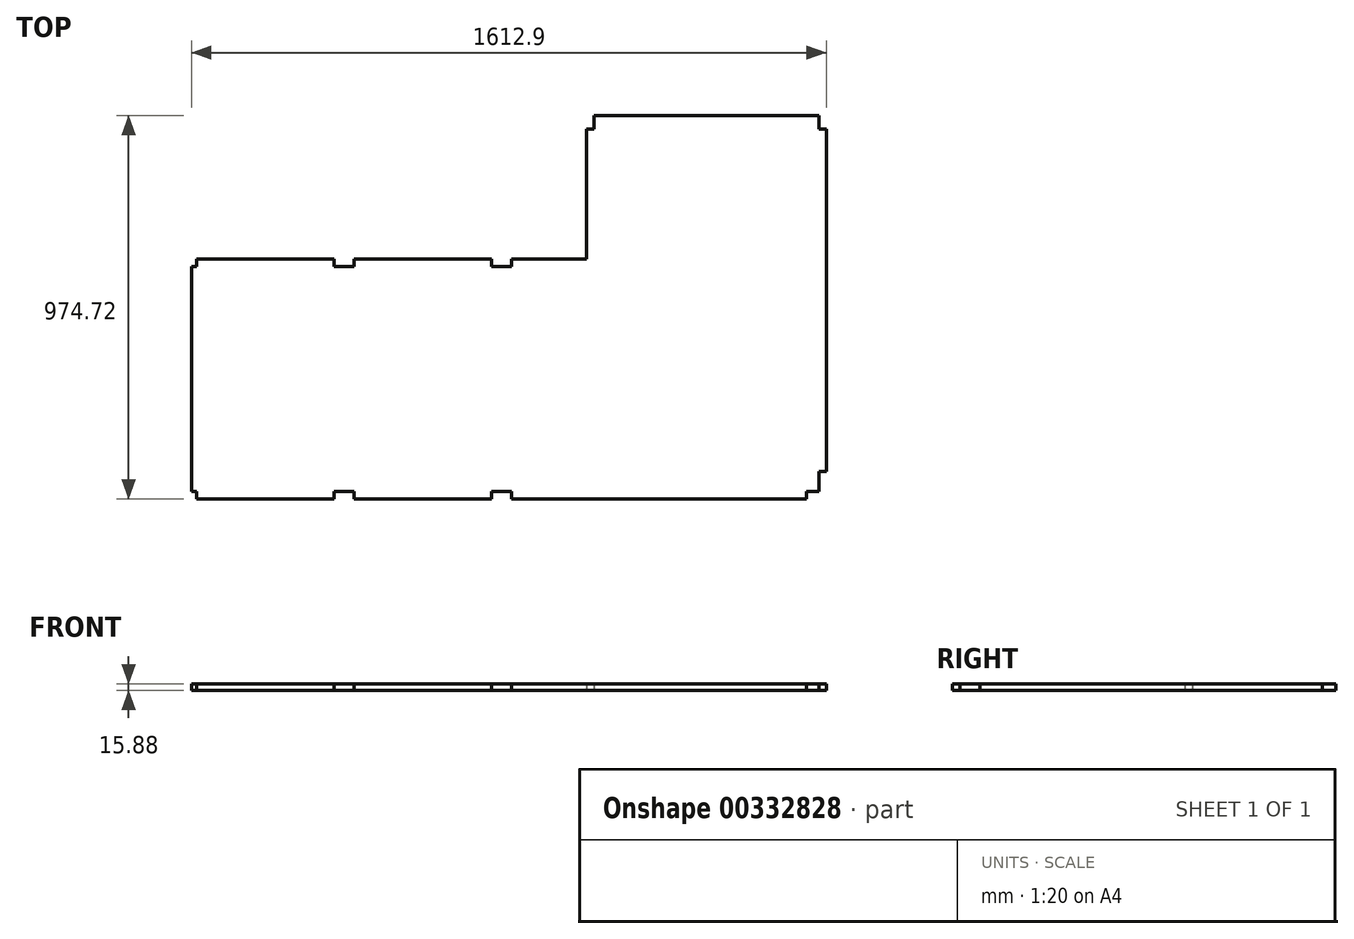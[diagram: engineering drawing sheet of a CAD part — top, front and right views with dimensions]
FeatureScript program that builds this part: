
annotation { "Feature Type Name" : "Feature", "Feature Type Description" : "" }
export const myFeature = defineFeature(function(context is Context, id is Id, definition is map)
    precondition{}
    {
        {
            var Q0;
            Q0=qCreatedBy(makeId("Top.planeOp"),FACE);
            var sketch = newSketch(context, id + "F0", { "sketchPlane" : qUnion([Q0])});
            skLineSegment(sketch, "E0.bottom", {"start": v(-50.8, 0) * mm, "end": v(-800.1, 0) * mm});
            skLineSegment(sketch, "E0.top", {"start": v(-19.05, 974.73) * mm, "end": v(-590.55, 974.72) * mm});
            skLineSegment(sketch, "E0.left", {"start": v(0, 69.85) * mm, "end": v(0, 939.8) * mm});
            skLineSegment(sketch, "E1.top", {"start": v(-1600.2, 609.6) * mm, "end": v(-1250.95, 609.6) * mm});
            skLineSegment(sketch, "E1.right", {"start": v(-609.6, 939.8) * mm, "end": v(-609.6, 609.6) * mm});
            skLineSegment(sketch, "E2.top", {"start": v(-1612.9, 590.55) * mm, "end": v(-1600.2, 590.55) * mm});
            skLineSegment(sketch, "E2.right", {"start": v(-1600.2, 609.6) * mm, "end": v(-1600.2, 590.55) * mm});
            skLineSegment(sketch, "E3.bottom", {"start": v(-1612.9, 19.05) * mm, "end": v(-1600.2, 19.05) * mm});
            skLineSegment(sketch, "E3.right", {"start": v(-1600.2, 19.05) * mm, "end": v(-1600.2, 0) * mm});
            skLineSegment(sketch, "E4.top", {"start": v(-609.6, 939.8) * mm, "end": v(-590.55, 939.8) * mm});
            skLineSegment(sketch, "E4.right", {"start": v(-590.55, 974.72) * mm, "end": v(-590.55, 939.8) * mm});
            skLineSegment(sketch, "E5.top", {"start": v(0, 939.8) * mm, "end": v(-19.05, 939.8) * mm});
            skLineSegment(sketch, "E5.right", {"start": v(-19.05, 974.73) * mm, "end": v(-19.05, 939.8) * mm});
            skLineSegment(sketch, "E6.top", {"start": v(-850.9, 590.55) * mm, "end": v(-800.1, 590.55) * mm});
            skLineSegment(sketch, "E6.left", {"start": v(-850.9, 609.6) * mm, "end": v(-850.9, 590.55) * mm});
            skLineSegment(sketch, "E6.right", {"start": v(-800.1, 609.6) * mm, "end": v(-800.1, 590.55) * mm});
            skLineSegment(sketch, "E7.trimOffspring", {"start": v(-800.1, 609.6) * mm, "end": v(-609.6, 609.6) * mm});
            skLineSegment(sketch, "E8.bottom", {"start": v(-850.9, 19.05) * mm, "end": v(-800.1, 19.05) * mm});
            skLineSegment(sketch, "E8.left", {"start": v(-850.9, 19.05) * mm, "end": v(-850.9, 0) * mm});
            skLineSegment(sketch, "E8.right", {"start": v(-800.1, 19.05) * mm, "end": v(-800.1, 0) * mm});
            skLineSegment(sketch, "E9.trimOffspring", {"start": v(-850.9, 0) * mm, "end": v(-1200.15, 0) * mm});
            skPoint(sketch, "E10.orphan", {"position": v(-800.1, -26.46) * mm});
            skLineSegment(sketch, "E11.top", {"start": v(-19.05, 19.05) * mm, "end": v(-50.8, 19.05) * mm});
            skLineSegment(sketch, "E11.right", {"start": v(-50.8, 0) * mm, "end": v(-50.8, 19.05) * mm});
            skLineSegment(sketch, "E12.top", {"start": v(-19.05, 69.85) * mm, "end": v(0, 69.85) * mm});
            skLineSegment(sketch, "E12.left", {"start": v(-19.05, 19.05) * mm, "end": v(-19.05, 69.85) * mm});
            skLineSegment(sketch, "E13", {"start": v(-1612.9, 590.55) * mm, "end": v(-1612.9, 19.05) * mm});
            skLineSegment(sketch, "E14.bottom", {"start": v(-1200.15, 590.55) * mm, "end": v(-1250.95, 590.55) * mm});
            skLineSegment(sketch, "E14.left", {"start": v(-1200.15, 590.55) * mm, "end": v(-1200.15, 609.6) * mm});
            skLineSegment(sketch, "E14.right", {"start": v(-1250.95, 590.55) * mm, "end": v(-1250.95, 609.6) * mm});
            skLineSegment(sketch, "E15.bottom", {"start": v(-1200.15, 19.05) * mm, "end": v(-1250.95, 19.05) * mm});
            skLineSegment(sketch, "E15.left", {"start": v(-1200.15, 19.05) * mm, "end": v(-1200.15, 0) * mm});
            skLineSegment(sketch, "E15.right", {"start": v(-1250.95, 19.05) * mm, "end": v(-1250.95, 0) * mm});
            skLineSegment(sketch, "E16.trimOffspring", {"start": v(-1200.15, 609.6) * mm, "end": v(-850.9, 609.6) * mm});
            skLineSegment(sketch, "E17.trimOffspring", {"start": v(-1250.95, 0) * mm, "end": v(-1600.2, 0) * mm});
            skPoint(sketch, "E18.orphan", {"position": v(-1200.15, -29.87) * mm});
            skSolve(sketch);
        }
        {
            var Q0;
            Q0 = qSketchRegion(id + "F0", true);
            extrude(context, id + "F1", {"entities" : qUnion([Q0]), "depth" : 15.88 * mm});
        }
    });
